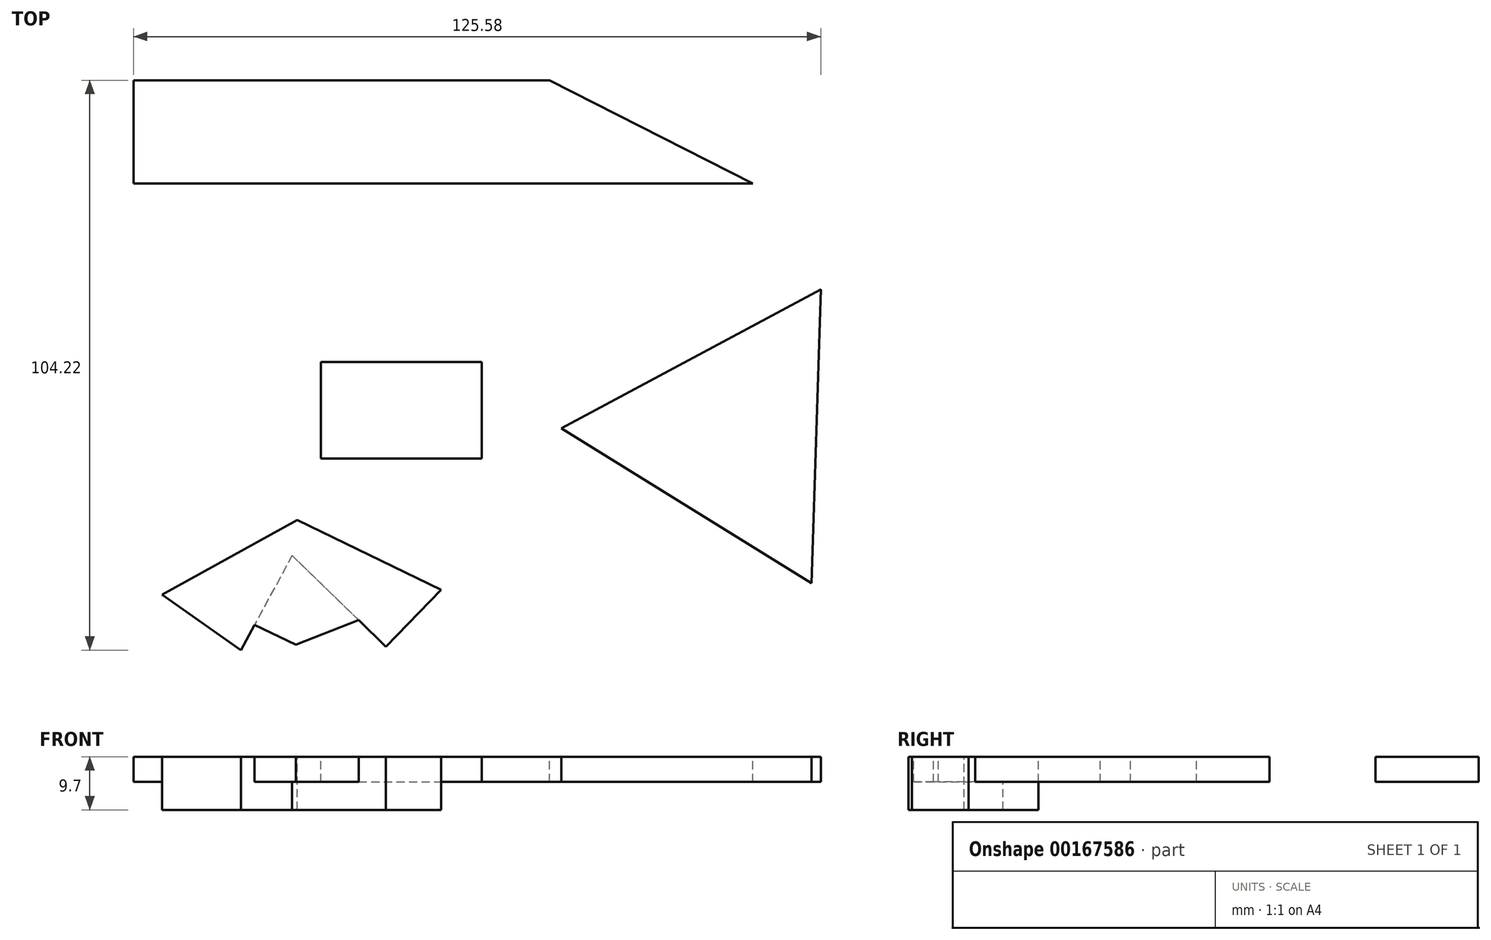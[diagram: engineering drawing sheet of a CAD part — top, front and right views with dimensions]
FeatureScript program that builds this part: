
annotation { "Feature Type Name" : "Feature", "Feature Type Description" : "" }
export const myFeature = defineFeature(function(context is Context, id is Id, definition is map)
    precondition{}
    {
        {
            var Q0;
            Q0=qCreatedBy(makeId("Top.planeOp"),FACE);
            var sketch = newSketch(context, id + "F0", { "sketchPlane" : qUnion([Q0])});
            skLineSegment(sketch, "E0", {"start": v(-68.43, 32.7) * mm, "end": v(44.7, 32.7) * mm});
            skLineSegment(sketch, "E1", {"start": v(44.7, 32.7) * mm, "end": v(34.37, 37.95) * mm});
            skLineSegment(sketch, "E2", {"start": v(7.6, 51.56) * mm, "end": v(-58.57, 51.56) * mm});
            skLineSegment(sketch, "E3", {"start": v(-58.57, 51.56) * mm, "end": v(-58.57, 32.7) * mm});
            skLineSegment(sketch, "E4.bottom", {"start": v(-34.2, 0) * mm, "end": v(-4.81, 0) * mm});
            skLineSegment(sketch, "E4.top", {"start": v(-34.2, -17.6) * mm, "end": v(-4.81, -17.6) * mm});
            skLineSegment(sketch, "E4.left", {"start": v(-34.2, 0) * mm, "end": v(-34.2, -17.6) * mm});
            skLineSegment(sketch, "E4.right", {"start": v(-4.81, 0) * mm, "end": v(-4.81, -17.6) * mm});
            skLineSegment(sketch, "E5", {"start": v(44.7, 32.7) * mm, "end": v(7.6, 51.56) * mm});
            skLineSegment(sketch, "E6", {"start": v(34.37, 37.95) * mm, "end": v(34.37, 37.95) * mm});
            skLineSegment(sketch, "E7", {"start": v(24.51, 42.96) * mm, "end": v(24.51, 42.96) * mm});
            skLineSegment(sketch, "E8", {"start": v(44.7, 32.7) * mm, "end": v(24.51, 42.96) * mm});
            skLineSegment(sketch, "E9", {"start": v(34.37, 37.95) * mm, "end": v(24.51, 42.96) * mm});
            skCircle(sketch, "E10.cCircle", {"center": v(40.79, -13.05) * mm, "radius": 15.52 * mm, "construction": true});
            skLineSegment(sketch, "E10.0", {"start": v(55.45, -40.41) * mm, "end": v(9.76, -12.07) * mm});
            skLineSegment(sketch, "E10.1", {"start": v(9.76, -12.07) * mm, "end": v(57.15, 13.33) * mm});
            skLineSegment(sketch, "E10.2", {"start": v(57.15, 13.33) * mm, "end": v(55.45, -40.41) * mm});
            skPoint(sketch, "E10.0.midPoint", {"position": v(32.6, -26.24) * mm});
            skLineSegment(sketch, "E11", {"start": v(-68.43, 32.7) * mm, "end": v(-68.43, 51.56) * mm});
            skLineSegment(sketch, "E12", {"start": v(-68.43, 51.56) * mm, "end": v(-58.57, 51.56) * mm});
            skLineSegment(sketch, "E13", {"start": v(-63.24, -42.5) * mm, "end": v(-48.8, -52.66) * mm});
            skLineSegment(sketch, "E14", {"start": v(-48.8, -52.66) * mm, "end": v(-39.45, -35.37) * mm});
            skLineSegment(sketch, "E15", {"start": v(-39.45, -35.37) * mm, "end": v(-22.32, -52.02) * mm});
            skLineSegment(sketch, "E16", {"start": v(-22.32, -52.02) * mm, "end": v(-12.22, -41.64) * mm});
            skLineSegment(sketch, "E17", {"start": v(-12.22, -41.64) * mm, "end": v(-38.5, -28.87) * mm});
            skLineSegment(sketch, "E18", {"start": v(-38.5, -28.87) * mm, "end": v(-63.24, -42.5) * mm});
            skLineSegment(sketch, "E19", {"start": v(-46.3, -48.04) * mm, "end": v(-38.8, -51.68) * mm});
            skLineSegment(sketch, "E20", {"start": v(-38.8, -51.68) * mm, "end": v(-27.3, -47.17) * mm});
            skSolve(sketch);
        }
        {
            var Q0;
            {var subQ5=sQuery(id+"F0.wireOp",EDGE,"E13");Q0=makeQuery(id+"F0.imprint","IMPRINT",FACE,{"disambiguationData":[TD([[makeQuery(id+"F0.imprint","IMPRINT",EDGE,{"derivedFrom":subQ5}),1.0]])]});}
            extrude(context, id + "F1", {"entities" : qUnion([Q0]), "oppositeDirection" : true, "depth" : 9.7 * mm});
        }
        {
            var Q0;
            Q0 = qSketchRegion(id + "F0", true);
            extrude(context, id + "F2", {"entities" : qUnion([Q0]), "operationType" : NewBodyOperationType.ADD, "oppositeDirection" : true, "depth" : 4.6 * mm});
        }
    });
